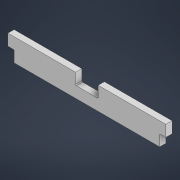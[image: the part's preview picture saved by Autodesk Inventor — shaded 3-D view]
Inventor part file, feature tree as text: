
AUTODESK INVENTOR PART (.ipt)
format: ipt  version: 2021 (Build 250183000, 183)  size: 136,704 bytes
history: native  units: mm
features: sketch x4, extrude x2, hole x2, plane x1, fillet x1, projected_geometry x1
ambient origin geometry x8: Origin, YZ Plane, XZ Plane, XY Plane, X Axis, Y Axis, Z Axis, Center Point
bodies: Solid1 (feature_tree)
feature tree (11):
  extrude  "Extrusion1"  Depth=384.0mm
  extrude  "Extrusion2"  Depth=369.0mm
  plane  "Work Plane1"
  fillet  "Fillet1"  Radius=10.0mm
  hole  "Hole1"  [1 undecoded]
  hole  "Hole2"  [1 undecoded]
  sketch  "Sketch1"  dims[d0=55.0mm d1=384.0mm]
  sketch  "Sketch2"  dims[d2=15.0mm d3=0.0mm d4=369.0mm]
  sketch  "Sketch3"  dims[d5=3.0mm d6=6.0mm d7=4.0mm d8=2.0mm d9=90.0deg d10=8.0mm d11=20.594885mm d12=10.0mm]
  projected_geometry  "Projected Loop1"
  sketch  "Sketch4"  dims[d13=3.0mm d14=6.0mm d15=4.0mm d16=2.0mm d17=90.0deg d18=8.0mm d19=20.594885mm d20=10.0mm d21=7.5mm d22=7.5mm d23=15.0mm d24=27.5mm d25=55.0mm d26=0.0mm d27=0.0mm d28=2.0mm]
note: 2 required parameter values undecoded (feature->parameter linkage not recoverable at this tier; creation-order binding heuristic only, values carry confidence <= 0.55)
